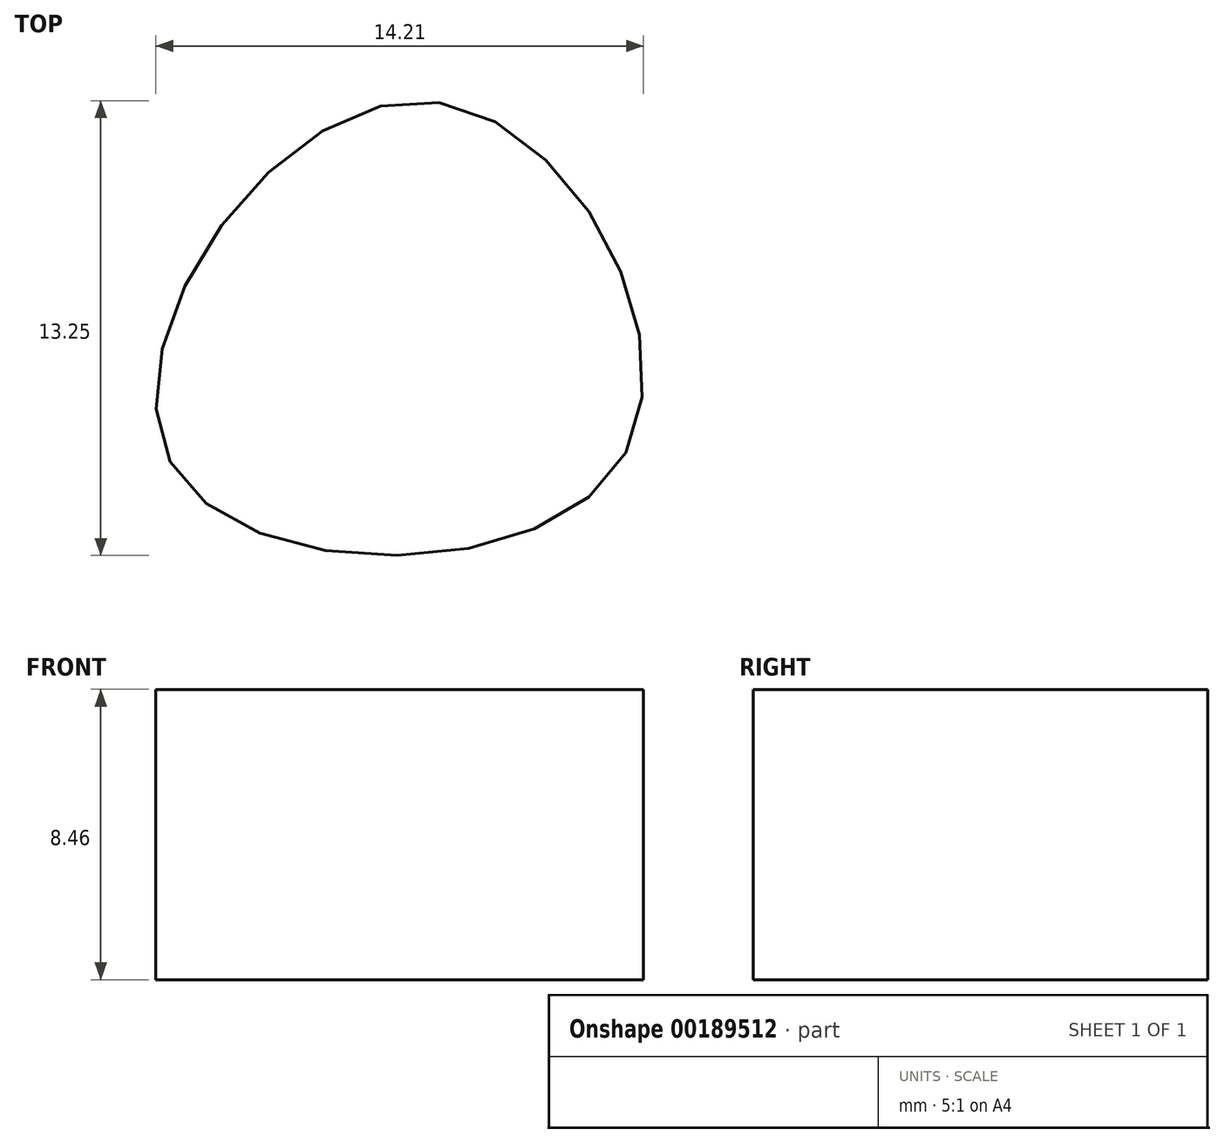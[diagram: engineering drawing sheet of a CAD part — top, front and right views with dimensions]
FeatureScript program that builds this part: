
annotation { "Feature Type Name" : "Feature", "Feature Type Description" : "" }
export const myFeature = defineFeature(function(context is Context, id is Id, definition is map)
    precondition{}
    {
        {
            var Q0;
            Q0=qCreatedBy(makeId("Top.planeOp"),FACE);
            var sketch = newSketch(context, id + "F0", { "sketchPlane" : qUnion([Q0])});
            skFitSpline(sketch, "E0", {"points": [v(0, 0) * mm, v(7.37, 10.52) * mm, v(13.12, 0) * mm, v(0, 0) * mm]});
            skSolve(sketch);
        }
        {
            var Q0;
            Q0=makeQuery(id+"F0.imprint","IMPRINT",FACE,{"disambiguationData":[TD([[makeQuery(id+"F0.imprint","IMPRINT",EDGE,{"derivedFrom":sQuery(id+"F0.wireOp",EDGE,"E0")}),-1.0]])]});
            extrude(context, id + "F1", {"entities" : qUnion([Q0]), "depth" : 8.46 * mm});
        }
    });
